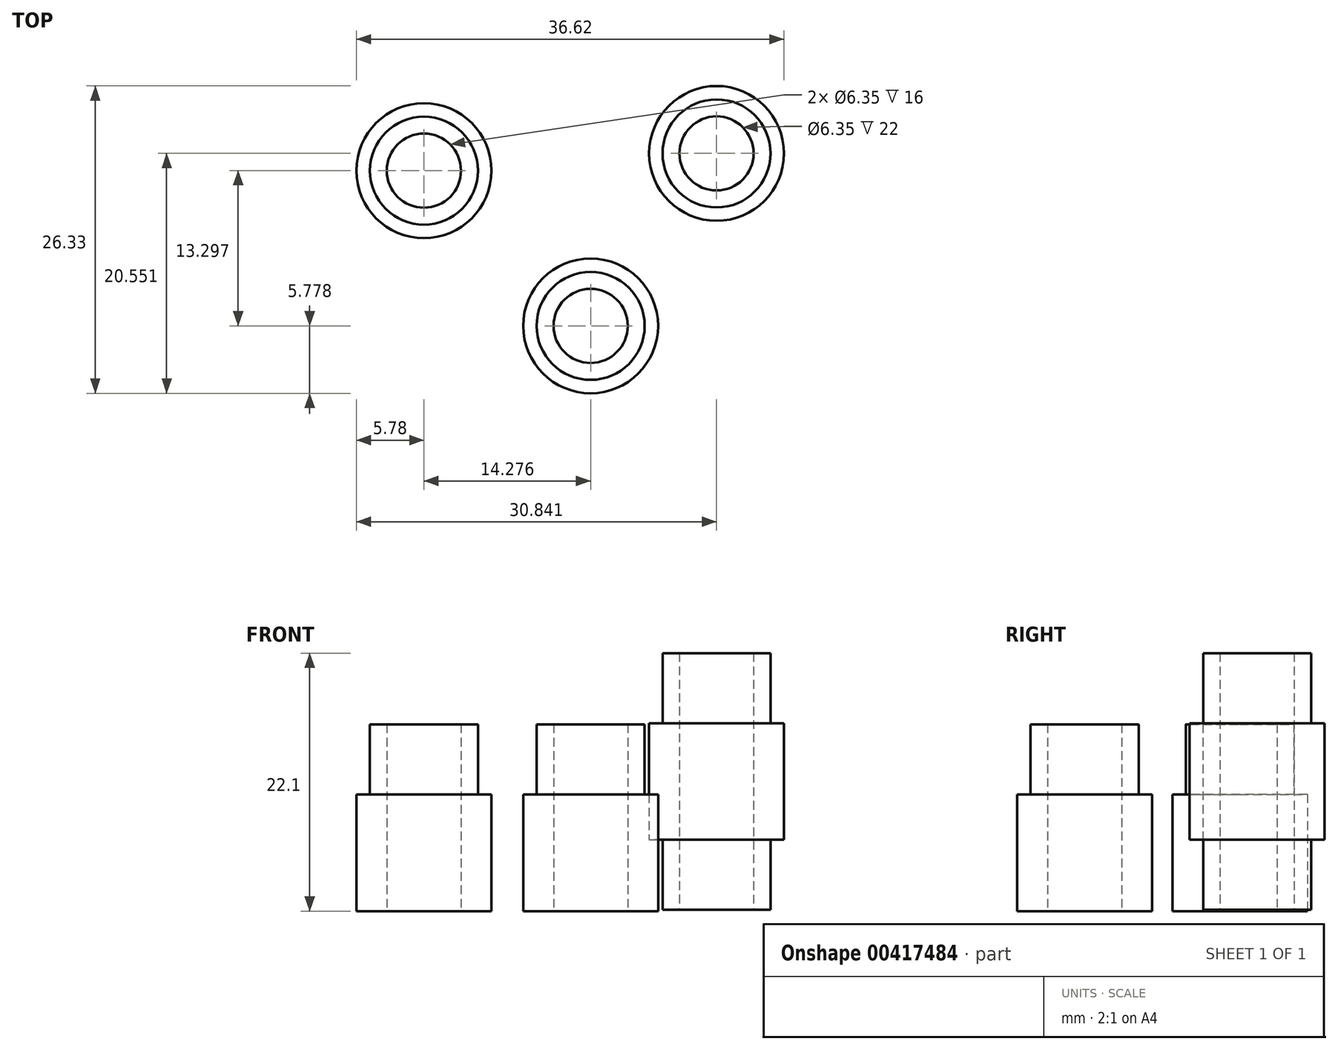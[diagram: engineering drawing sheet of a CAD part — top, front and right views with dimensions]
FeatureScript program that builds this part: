
annotation { "Feature Type Name" : "Feature", "Feature Type Description" : "" }
export const myFeature = defineFeature(function(context is Context, id is Id, definition is map)
    precondition{}
    {
        {
            var Q0;
            Q0=qCreatedBy(makeId("Top.planeOp"),FACE);
            var sketch = newSketch(context, id + "F0", { "sketchPlane" : qUnion([Q0])});
            skCircle(sketch, "E0", {"center": v(-47.26, -15.8) * mm, "radius": 5.78 * mm});
            skCircle(sketch, "E1", {"center": v(-47.26, -15.8) * mm, "radius": 4.62 * mm});
            skCircle(sketch, "E2", {"center": v(-47.26, -15.8) * mm, "radius": 3.17 * mm});
            skCircle(sketch, "E3", {"center": v(-22.2, -14.33) * mm, "radius": 5.78 * mm});
            skCircle(sketch, "E4", {"center": v(-22.2, -14.33) * mm, "radius": 4.62 * mm});
            skCircle(sketch, "E5", {"center": v(-22.2, -14.33) * mm, "radius": 3.17 * mm});
            skCircle(sketch, "E6", {"center": v(-32.98, -29.1) * mm, "radius": 5.78 * mm});
            skCircle(sketch, "E7", {"center": v(-32.98, -29.1) * mm, "radius": 4.62 * mm});
            skCircle(sketch, "E8", {"center": v(-32.98, -29.1) * mm, "radius": 3.17 * mm});
            skSolve(sketch);
        }
        {
            var Q0;
            Q0=makeQuery(id+"F0.imprint","IMPRINT",FACE,{"disambiguationData":[TD([[makeQuery(id+"F0.imprint","IMPRINT",EDGE,{"derivedFrom":sQuery(id+"F0.wireOp",EDGE,"E1")}),1.0]])]});
            extrude(context, id + "F1", {"entities" : qUnion([Q0]), "depth" : 16 * mm});
        }
        {
            var Q0;
            Q0=makeQuery(id+"F0.imprint","IMPRINT",FACE,{"disambiguationData":[TD([[makeQuery(id+"F0.imprint","IMPRINT",EDGE,{"derivedFrom":sQuery(id+"F0.wireOp",EDGE,"E0")}),1.0]])]});
            extrude(context, id + "F2", {"entities" : qUnion([Q0]), "operationType" : NewBodyOperationType.ADD, "depth" : 10 * mm});
        }
        {
            var Q0;
            Q0=makeQuery(id+"F0.imprint","IMPRINT",FACE,{"disambiguationData":[TD([[makeQuery(id+"F0.imprint","IMPRINT",EDGE,{"derivedFrom":sQuery(id+"F0.wireOp",EDGE,"E7")}),1.0]])]});
            extrude(context, id + "F3", {"entities" : qUnion([Q0]), "depth" : 16 * mm});
        }
        {
            var Q0;
            Q0=makeQuery(id+"F0.imprint","IMPRINT",FACE,{"disambiguationData":[TD([[makeQuery(id+"F0.imprint","IMPRINT",EDGE,{"derivedFrom":sQuery(id+"F0.wireOp",EDGE,"E6")}),1.0]])]});
            var Q1;
            Q1=sQuery(id+"F0.wireOp",EDGE,"E6");
            extrude(context, id + "F4", {"entities" : qUnion([Q0]), "operationType" : NewBodyOperationType.ADD, "surfaceEntities" : qUnion([Q1]), "depth" : 10 * mm});
        }
        {
            var Q0;
            Q0=makeQuery(id+"F0.imprint","IMPRINT",FACE,{"disambiguationData":[TD([[makeQuery(id+"F0.imprint","IMPRINT",EDGE,{"derivedFrom":sQuery(id+"F0.wireOp",EDGE,"E4")}),1.0]])]});
            extrude(context, id + "F5", {"entities" : qUnion([Q0]), "endBound" : BoundingType.SYMMETRIC, "depth" : 22 * mm});
        }
        {
            var Q0;
            Q0=makeQuery(id+"F0.imprint","IMPRINT",FACE,{"disambiguationData":[TD([[makeQuery(id+"F0.imprint","IMPRINT",EDGE,{"derivedFrom":sQuery(id+"F0.wireOp",EDGE,"E3")}),1.0]])]});
            extrude(context, id + "F6", {"entities" : qUnion([Q0]), "operationType" : NewBodyOperationType.ADD, "endBound" : BoundingType.SYMMETRIC, "depth" : 10 * mm});
        }
        {
            var Q0;
            Q0=makeQuery(id+"F5.opExtrude","SWEPT_BODY",BODY,{"disambiguationData":[OSD([sQuery(id+"F0.wireOp",EDGE,"E4"),sQuery(id+"F0.wireOp",EDGE,"E5")])]});
            transform(context, id + "F7", {"entities" : qUnion([Q0]), "transformType" : TransformType.TRANSLATION_3D, "dx" : 0 * mm, "dy" : 0 * mm, "dz" : 11.1 * mm, "makeCopy" : false});
        }
    });
